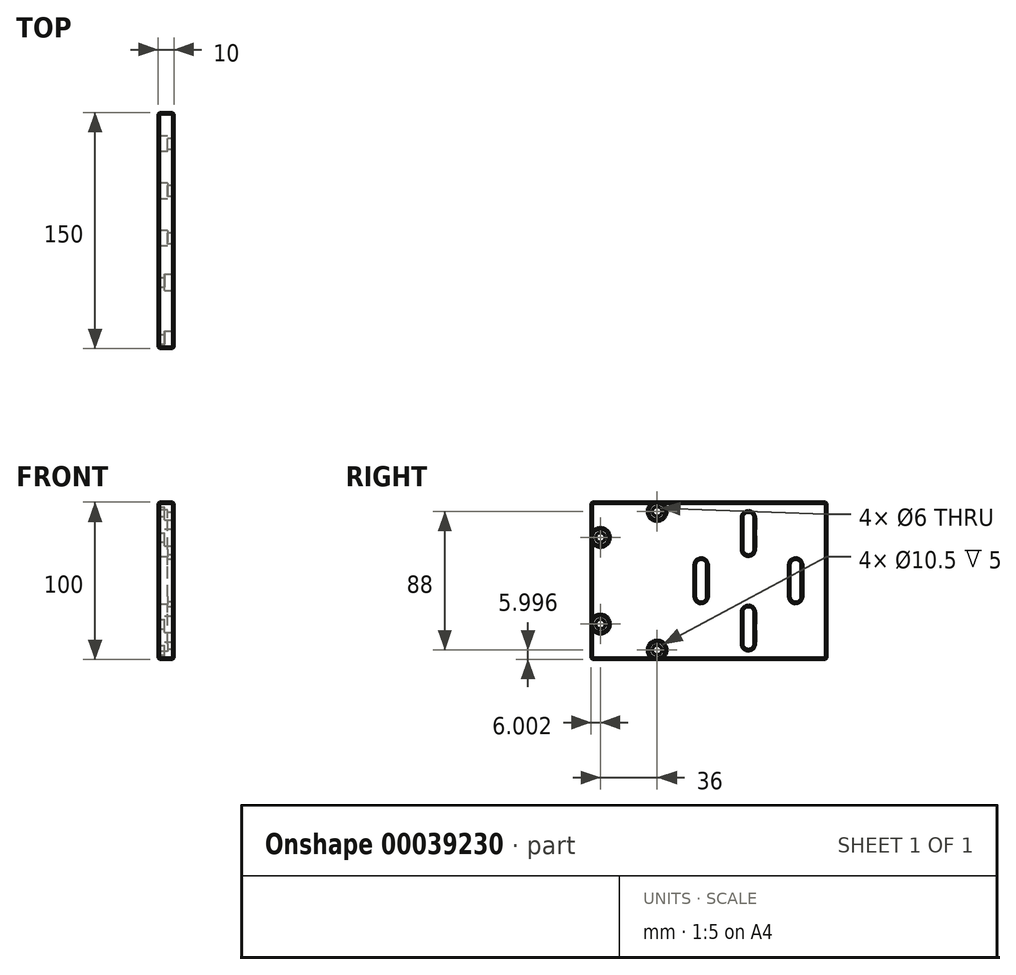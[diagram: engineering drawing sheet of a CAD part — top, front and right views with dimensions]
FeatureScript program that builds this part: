
annotation { "Feature Type Name" : "Feature", "Feature Type Description" : "" }
export const myFeature = defineFeature(function(context is Context, id is Id, definition is map)
    precondition{}
    {
        {
            var Q0;
            Q0=qCreatedBy(makeId("Right.planeOp"),FACE);
            var sketch = newSketch(context, id + "F0", { "sketchPlane" : qUnion([Q0])});
            skLineSegment(sketch, "E0.bottom", {"start": v(-58.68, 47.94) * mm, "end": v(91.32, 47.94) * mm});
            skLineSegment(sketch, "E0.top", {"start": v(-58.68, -52.06) * mm, "end": v(91.32, -52.06) * mm});
            skLineSegment(sketch, "E0.left", {"start": v(-58.68, 47.94) * mm, "end": v(-58.68, -52.06) * mm});
            skLineSegment(sketch, "E0.right", {"start": v(91.32, 47.94) * mm, "end": v(91.32, -52.06) * mm});
            skSolve(sketch);
        }
        {
            var Q0;
            Q0=makeQuery(id+"F0.imprint","IMPRINT",FACE,{"disambiguationData":[TD([[makeQuery(id+"F0.imprint","IMPRINT",EDGE,{"derivedFrom":sQuery(id+"F0.wireOp",EDGE,"E0.bottom")}),-1.0]])]});
            extrude(context, id + "F1", {"entities" : qUnion([Q0]), "depth" : 10 * mm});
        }
        {
            var Q0;
            Q0=makeQuery(id+"F1.opExtrude","CAP_FACE",FACE,{"disambiguationData":[OSD([sQuery(id+"F0.wireOp",EDGE,"E0.bottom"),sQuery(id+"F0.wireOp",EDGE,"E0.top"),sQuery(id+"F0.wireOp",EDGE,"E0.left"),sQuery(id+"F0.wireOp",EDGE,"E0.right")])],"isStart":false});
            var sketch = newSketch(context, id + "F2", { "sketchPlane" : qUnion([Q0])});
            skPoint(sketch, "E1", {"position": v(-52.68, 25.44) * mm});
            skPoint(sketch, "E2", {"position": v(-52.68, -29.56) * mm});
            skPoint(sketch, "E3", {"position": v(-16.68, 41.94) * mm});
            skPoint(sketch, "E4", {"position": v(-16.68, -46.06) * mm});
            skSolve(sketch);
        }
        {
            var Q0;
            Q0=sQuery(id+"F2.wireOp",VERTEX,"E3");
            var Q1;
            Q1=sQuery(id+"F2.wireOp",VERTEX,"E1");
            var Q2;
            Q2=sQuery(id+"F2.wireOp",VERTEX,"E2");
            var Q3;
            Q3=sQuery(id+"F2.wireOp",VERTEX,"E4");
            var Q4;
            Q4=makeQuery(id+"F1.opExtrude","SWEPT_BODY",BODY,{"disambiguationData":[OSD([sQuery(id+"F0.wireOp",EDGE,"E0.bottom"),sQuery(id+"F0.wireOp",EDGE,"E0.top"),sQuery(id+"F0.wireOp",EDGE,"E0.left"),sQuery(id+"F0.wireOp",EDGE,"E0.right")])]});
            hole(context, id + "F3", {"style" : HoleStyle.C_BORE, "holeDiameter" : 6 * mm, "cBoreDiameter" : 10.5 * mm, "cBoreDepth" : 6 * mm, "endStyle" : HoleEndStyle.THROUGH, "locations" : qUnion([Q0, Q1, Q2, Q3]), "scope" : qUnion([Q4])});
        }
        {
            var Q0;
            Q0=makeQuery(id+"F1.opExtrude","CAP_FACE",FACE,{"disambiguationData":[OSD([sQuery(id+"F0.wireOp",EDGE,"E0.bottom"),sQuery(id+"F0.wireOp",EDGE,"E0.top"),sQuery(id+"F0.wireOp",EDGE,"E0.left"),sQuery(id+"F0.wireOp",EDGE,"E0.right")])],"isStart":true});
            var sketch = newSketch(context, id + "F4", { "sketchPlane" : qUnion([Q0])});
            skPoint(sketch, "E5", {"position": v(-41.32, -2.06) * mm});
            skPoint(sketch, "E5.positionSnap0", {"position": v(-91.32, -2.06) * mm});
            skPoint(sketch, "E6", {"position": v(-11.32, -2.06) * mm});
            skPoint(sketch, "E7", {"position": v(-71.32, -2.06) * mm});
            skPoint(sketch, "E8", {"position": v(-41.32, 27.94) * mm});
            skPoint(sketch, "E9", {"position": v(-41.32, -32.06) * mm});
            skSolve(sketch);
        }
        {
            var Q0;
            {var subQ0=sQuery(id+"F0.wireOp",EDGE,"E0.bottom");Q0=makeQuery(id+"F4.imprint","IMPRINT",FACE,{"disambiguationData":[TD([[makeQuery(id+"F4.imprint","IMPRINT",EDGE,{"derivedFrom":makeQuery(id+"F1.opExtrude","CAP_EDGE",EDGE,{"disambiguationData":[OSD([subQ0])],"isStart":true})}),1.0]])]});}
            var sketch = newSketch(context, id + "F5", { "sketchPlane" : qUnion([Q0])});
            skLineSegment(sketch, "E10.left", {"start": v(-44.82, 37.94) * mm, "end": v(-44.82, 17.94) * mm});
            skLineSegment(sketch, "E10.right", {"start": v(-37.82, 37.94) * mm, "end": v(-37.82, 17.94) * mm});
            skArc(sketch, "E11", {"start": v(-37.82, 37.94) * mm, "mid": v(-41.32, 41.44) * mm, "end": v(-44.82, 37.94) * mm});
            skArc(sketch, "E12", {"start": v(-44.82, 17.94) * mm, "mid": v(-41.32, 14.44) * mm, "end": v(-37.82, 17.94) * mm});
            skArc(sketch, "E13", {"start": v(-67.82, 7.94) * mm, "mid": v(-71.32, 11.44) * mm, "end": v(-74.82, 7.94) * mm});
            skLineSegment(sketch, "E14.right", {"start": v(-67.82, 7.94) * mm, "end": v(-67.82, -12.06) * mm});
            skArc(sketch, "E15", {"start": v(-74.82, -12.06) * mm, "mid": v(-71.32, -15.56) * mm, "end": v(-67.82, -12.06) * mm});
            skLineSegment(sketch, "E14.left", {"start": v(-74.82, 7.94) * mm, "end": v(-74.82, -12.06) * mm});
            skArc(sketch, "E16", {"start": v(-7.82, 7.94) * mm, "mid": v(-11.32, 11.44) * mm, "end": v(-14.82, 7.94) * mm});
            skLineSegment(sketch, "E17.right", {"start": v(-7.82, 7.94) * mm, "end": v(-7.82, -12.06) * mm});
            skArc(sketch, "E18", {"start": v(-14.82, -12.06) * mm, "mid": v(-11.32, -15.56) * mm, "end": v(-7.82, -12.06) * mm});
            skLineSegment(sketch, "E17.left", {"start": v(-14.82, 7.94) * mm, "end": v(-14.82, -12.06) * mm});
            skArc(sketch, "E19", {"start": v(-37.82, -22.06) * mm, "mid": v(-41.32, -18.56) * mm, "end": v(-44.82, -22.06) * mm});
            skLineSegment(sketch, "E20.right", {"start": v(-37.82, -22.06) * mm, "end": v(-37.82, -42.06) * mm});
            skArc(sketch, "E21", {"start": v(-44.82, -42.06) * mm, "mid": v(-41.32, -45.56) * mm, "end": v(-37.82, -42.06) * mm});
            skLineSegment(sketch, "E20.left", {"start": v(-44.82, -22.06) * mm, "end": v(-44.82, -42.06) * mm});
            skSolve(sketch);
        }
        {
            var Q0;
            Q0=makeQuery(id+"F5.imprint","IMPRINT",FACE,{"disambiguationData":[TD([[makeQuery(id+"F5.imprint","IMPRINT",EDGE,{"derivedFrom":sQuery(id+"F5.wireOp",EDGE,"E13")}),1.0]])]});
            var Q1;
            Q1=makeQuery(id+"F5.imprint","IMPRINT",FACE,{"disambiguationData":[TD([[makeQuery(id+"F5.imprint","IMPRINT",EDGE,{"derivedFrom":sQuery(id+"F5.wireOp",EDGE,"E16")}),1.0]])]});
            var Q2;
            Q2=makeQuery(id+"F5.imprint","IMPRINT",FACE,{"disambiguationData":[TD([[makeQuery(id+"F5.imprint","IMPRINT",EDGE,{"derivedFrom":sQuery(id+"F5.wireOp",EDGE,"E19")}),1.0]])]});
            var Q3;
            Q3=makeQuery(id+"F5.imprint","IMPRINT",FACE,{"disambiguationData":[TD([[makeQuery(id+"F5.imprint","IMPRINT",EDGE,{"derivedFrom":sQuery(id+"F5.wireOp",EDGE,"E10.left")}),1.0]])]});
            extrude(context, id + "F6", {"entities" : qUnion([Q0, Q1, Q2, Q3]), "operationType" : NewBodyOperationType.REMOVE, "endBound" : BoundingType.THROUGH_ALL, "oppositeDirection" : true, "depth" : 25 * mm});
        }
        {
            var Q0;
            {var subQ0=sQuery(id+"F0.wireOp",EDGE,"E0.bottom");Q0=makeQuery(id+"F4.imprint","IMPRINT",FACE,{"disambiguationData":[TD([[makeQuery(id+"F4.imprint","IMPRINT",EDGE,{"derivedFrom":makeQuery(id+"F1.opExtrude","CAP_EDGE",EDGE,{"disambiguationData":[OSD([subQ0])],"isStart":true})}),1.0]])]});}
            var sketch = newSketch(context, id + "F7", { "sketchPlane" : qUnion([Q0])});
            skLineSegment(sketch, "E22.left", {"start": v(-76.32, 7.94) * mm, "end": v(-76.32, -12.06) * mm});
            skLineSegment(sketch, "E22.right", {"start": v(-66.32, 7.94) * mm, "end": v(-66.32, -12.06) * mm});
            skArc(sketch, "E23", {"start": v(-66.32, 7.94) * mm, "mid": v(-71.32, 12.94) * mm, "end": v(-76.32, 7.94) * mm});
            skArc(sketch, "E24", {"start": v(-76.32, -12.06) * mm, "mid": v(-71.32, -17.06) * mm, "end": v(-66.32, -12.06) * mm});
            skLineSegment(sketch, "E25.right", {"start": v(-36.32, -22.06) * mm, "end": v(-36.32, -42.06) * mm});
            skLineSegment(sketch, "E25.left", {"start": v(-46.32, -22.06) * mm, "end": v(-46.32, -42.06) * mm});
            skArc(sketch, "E26", {"start": v(-46.32, -42.06) * mm, "mid": v(-41.32, -47.06) * mm, "end": v(-36.32, -42.06) * mm});
            skArc(sketch, "E27", {"start": v(-36.32, -22.06) * mm, "mid": v(-41.32, -17.06) * mm, "end": v(-46.32, -22.06) * mm});
            skLineSegment(sketch, "E28.right", {"start": v(-6.32, 7.94) * mm, "end": v(-6.32, -12.06) * mm});
            skLineSegment(sketch, "E28.left", {"start": v(-16.32, 7.94) * mm, "end": v(-16.32, -12.06) * mm});
            skArc(sketch, "E29", {"start": v(-16.32, -12.06) * mm, "mid": v(-11.32, -17.06) * mm, "end": v(-6.32, -12.06) * mm});
            skArc(sketch, "E30", {"start": v(-6.32, 7.94) * mm, "mid": v(-11.32, 12.94) * mm, "end": v(-16.32, 7.94) * mm});
            skLineSegment(sketch, "E31.right", {"start": v(-36.32, 37.94) * mm, "end": v(-36.32, 17.94) * mm});
            skLineSegment(sketch, "E31.left", {"start": v(-46.32, 37.94) * mm, "end": v(-46.32, 17.94) * mm});
            skArc(sketch, "E32", {"start": v(-46.32, 17.94) * mm, "mid": v(-41.32, 12.94) * mm, "end": v(-36.32, 17.94) * mm});
            skArc(sketch, "E33", {"start": v(-36.32, 37.94) * mm, "mid": v(-41.32, 42.94) * mm, "end": v(-46.32, 37.94) * mm});
            skSolve(sketch);
        }
        {
            var Q0;
            Q0 = qSketchRegion(id + "F7", true);
            extrude(context, id + "F8", {"entities" : qUnion([Q0]), "operationType" : NewBodyOperationType.REMOVE, "oppositeDirection" : true, "depth" : 6 * mm});
        }
        {
            var Q0;
            Q0=makeQuery(id+"F1.opExtrude","CAP_EDGE",EDGE,{"disambiguationData":[OSD([sQuery(id+"F0.wireOp",EDGE,"E0.right")])],"isStart":true});
            var Q1;
            Q1=makeQuery(id+"F1.opExtrude","CAP_EDGE",EDGE,{"disambiguationData":[OSD([sQuery(id+"F0.wireOp",EDGE,"E0.right")])],"isStart":false});
            var Q2;
            Q2=makeQuery(id+"F1.opExtrude","SWEPT_EDGE",EDGE,{"disambiguationData":[OSD([sQuery(id+"F0.wireOp",EDGE,"E0.top"),sQuery(id+"F0.wireOp",EDGE,"E0.right")])]});
            var Q3;
            Q3=makeQuery(id+"F1.opExtrude","CAP_EDGE",EDGE,{"disambiguationData":[OSD([sQuery(id+"F0.wireOp",EDGE,"E0.top")])],"isStart":true});
            var Q4;
            Q4=makeQuery(id+"F1.opExtrude","CAP_EDGE",EDGE,{"disambiguationData":[OSD([sQuery(id+"F0.wireOp",EDGE,"E0.top")])],"isStart":false});
            var Q5;
            Q5=makeQuery(id+"F1.opExtrude","CAP_EDGE",EDGE,{"disambiguationData":[OSD([sQuery(id+"F0.wireOp",EDGE,"E0.bottom")])],"isStart":true});
            var Q6;
            Q6=makeQuery(id+"F1.opExtrude","SWEPT_EDGE",EDGE,{"disambiguationData":[OSD([sQuery(id+"F0.wireOp",EDGE,"E0.bottom"),sQuery(id+"F0.wireOp",EDGE,"E0.right")])]});
            var Q7;
            Q7=makeQuery(id+"F8.boolean.opBoolean","COPY",EDGE,{"derivedFrom":makeQuery(id+"F8.opExtrude","CAP_EDGE",EDGE,{"disambiguationData":[OSD([sQuery(id+"F7.wireOp",EDGE,"E22.right")])],"isStart":true})});
            var Q8;
            Q8=makeQuery(id+"F8.boolean.opBoolean","COPY",EDGE,{"derivedFrom":makeQuery(id+"F8.opExtrude","CAP_EDGE",EDGE,{"disambiguationData":[OSD([sQuery(id+"F7.wireOp",EDGE,"E22.left")])],"isStart":true})});
            var Q9;
            Q9=makeQuery(id+"F8.boolean.opBoolean","COPY",EDGE,{"derivedFrom":makeQuery(id+"F8.opExtrude","CAP_EDGE",EDGE,{"disambiguationData":[OSD([sQuery(id+"F7.wireOp",EDGE,"E23")])],"isStart":true})});
            var Q10;
            Q10=makeQuery(id+"F8.boolean.opBoolean","COPY",EDGE,{"derivedFrom":makeQuery(id+"F8.opExtrude","CAP_EDGE",EDGE,{"disambiguationData":[OSD([sQuery(id+"F7.wireOp",EDGE,"E24")])],"isStart":true})});
            var Q11;
            Q11=makeQuery(id+"F8.boolean.opBoolean","COPY",EDGE,{"derivedFrom":makeQuery(id+"F8.opExtrude","CAP_EDGE",EDGE,{"disambiguationData":[OSD([sQuery(id+"F7.wireOp",EDGE,"E31.left")])],"isStart":true})});
            var Q12;
            Q12=makeQuery(id+"F8.boolean.opBoolean","COPY",EDGE,{"derivedFrom":makeQuery(id+"F8.opExtrude","CAP_EDGE",EDGE,{"disambiguationData":[OSD([sQuery(id+"F7.wireOp",EDGE,"E31.right")])],"isStart":true})});
            var Q13;
            Q13=makeQuery(id+"F8.boolean.opBoolean","COPY",EDGE,{"derivedFrom":makeQuery(id+"F8.opExtrude","CAP_EDGE",EDGE,{"disambiguationData":[OSD([sQuery(id+"F7.wireOp",EDGE,"E33")])],"isStart":true})});
            var Q14;
            Q14=makeQuery(id+"F8.boolean.opBoolean","COPY",EDGE,{"derivedFrom":makeQuery(id+"F8.opExtrude","CAP_EDGE",EDGE,{"disambiguationData":[OSD([sQuery(id+"F7.wireOp",EDGE,"E32")])],"isStart":true})});
            var Q15;
            Q15=makeQuery(id+"F8.boolean.opBoolean","COPY",EDGE,{"derivedFrom":makeQuery(id+"F8.opExtrude","CAP_EDGE",EDGE,{"disambiguationData":[OSD([sQuery(id+"F7.wireOp",EDGE,"E25.right")])],"isStart":true})});
            var Q16;
            Q16=makeQuery(id+"F8.boolean.opBoolean","COPY",EDGE,{"derivedFrom":makeQuery(id+"F8.opExtrude","CAP_EDGE",EDGE,{"disambiguationData":[OSD([sQuery(id+"F7.wireOp",EDGE,"E27")])],"isStart":true})});
            var Q17;
            Q17=makeQuery(id+"F8.boolean.opBoolean","COPY",EDGE,{"derivedFrom":makeQuery(id+"F8.opExtrude","CAP_EDGE",EDGE,{"disambiguationData":[OSD([sQuery(id+"F7.wireOp",EDGE,"E25.left")])],"isStart":true})});
            var Q18;
            Q18=makeQuery(id+"F8.boolean.opBoolean","COPY",EDGE,{"derivedFrom":makeQuery(id+"F8.opExtrude","CAP_EDGE",EDGE,{"disambiguationData":[OSD([sQuery(id+"F7.wireOp",EDGE,"E26")])],"isStart":true})});
            var Q19;
            Q19=makeQuery(id+"F8.boolean.opBoolean","COPY",EDGE,{"derivedFrom":makeQuery(id+"F8.opExtrude","CAP_EDGE",EDGE,{"disambiguationData":[OSD([sQuery(id+"F7.wireOp",EDGE,"E29")])],"isStart":true})});
            var Q20;
            Q20=makeQuery(id+"F8.boolean.opBoolean","COPY",EDGE,{"derivedFrom":makeQuery(id+"F8.opExtrude","CAP_EDGE",EDGE,{"disambiguationData":[OSD([sQuery(id+"F7.wireOp",EDGE,"E28.right")])],"isStart":true})});
            var Q21;
            Q21=makeQuery(id+"F8.boolean.opBoolean","COPY",EDGE,{"derivedFrom":makeQuery(id+"F8.opExtrude","CAP_EDGE",EDGE,{"disambiguationData":[OSD([sQuery(id+"F7.wireOp",EDGE,"E28.left")])],"isStart":true})});
            var Q22;
            Q22=makeQuery(id+"F8.boolean.opBoolean","COPY",EDGE,{"derivedFrom":makeQuery(id+"F8.opExtrude","CAP_EDGE",EDGE,{"disambiguationData":[OSD([sQuery(id+"F7.wireOp",EDGE,"E30")])],"isStart":true})});
            var Q23;
            Q23=makeQuery(id+"F3.hole-0.boolean.opBoolean","INTERSECT",EDGE,{"derivedFrom":[makeQuery(id+"F1.opExtrude","CAP_FACE",FACE,{"disambiguationData":[OSD([sQuery(id+"F0.wireOp",EDGE,"E0.bottom"),sQuery(id+"F0.wireOp",EDGE,"E0.top"),sQuery(id+"F0.wireOp",EDGE,"E0.left"),sQuery(id+"F0.wireOp",EDGE,"E0.right")])],"isStart":true}),makeQuery(id+"F3.hole-0.opRevolve","SWEPT_FACE",FACE,{"disambiguationData":[OSD([sQuery(id+"F3.hole-0.sketch.wireOp",EDGE,"core_line_2")])]})]});
            var Q24;
            Q24=makeQuery(id+"F3.hole-1.boolean.opBoolean","INTERSECT",EDGE,{"derivedFrom":[makeQuery(id+"F1.opExtrude","CAP_FACE",FACE,{"disambiguationData":[OSD([sQuery(id+"F0.wireOp",EDGE,"E0.bottom"),sQuery(id+"F0.wireOp",EDGE,"E0.top"),sQuery(id+"F0.wireOp",EDGE,"E0.left"),sQuery(id+"F0.wireOp",EDGE,"E0.right")])],"isStart":true}),makeQuery(id+"F3.hole-1.opRevolve","SWEPT_FACE",FACE,{"disambiguationData":[OSD([sQuery(id+"F3.hole-1.sketch.wireOp",EDGE,"core_line_2")])]})]});
            var Q25;
            Q25=makeQuery(id+"F3.hole-2.boolean.opBoolean","INTERSECT",EDGE,{"derivedFrom":[makeQuery(id+"F1.opExtrude","CAP_FACE",FACE,{"disambiguationData":[OSD([sQuery(id+"F0.wireOp",EDGE,"E0.bottom"),sQuery(id+"F0.wireOp",EDGE,"E0.top"),sQuery(id+"F0.wireOp",EDGE,"E0.left"),sQuery(id+"F0.wireOp",EDGE,"E0.right")])],"isStart":true}),makeQuery(id+"F3.hole-2.opRevolve","SWEPT_FACE",FACE,{"disambiguationData":[OSD([sQuery(id+"F3.hole-2.sketch.wireOp",EDGE,"core_line_2")])]})]});
            var Q26;
            Q26=makeQuery(id+"F3.hole-3.boolean.opBoolean","INTERSECT",EDGE,{"derivedFrom":[makeQuery(id+"F1.opExtrude","CAP_FACE",FACE,{"disambiguationData":[OSD([sQuery(id+"F0.wireOp",EDGE,"E0.bottom"),sQuery(id+"F0.wireOp",EDGE,"E0.top"),sQuery(id+"F0.wireOp",EDGE,"E0.left"),sQuery(id+"F0.wireOp",EDGE,"E0.right")])],"isStart":true}),makeQuery(id+"F3.hole-3.opRevolve","SWEPT_FACE",FACE,{"disambiguationData":[OSD([sQuery(id+"F3.hole-3.sketch.wireOp",EDGE,"core_line_2")])]})]});
            var Q27;
            Q27=makeQuery(id+"F1.opExtrude","SWEPT_EDGE",EDGE,{"disambiguationData":[OSD([sQuery(id+"F0.wireOp",EDGE,"E0.top"),sQuery(id+"F0.wireOp",EDGE,"E0.left")])]});
            var Q28;
            Q28=makeQuery(id+"F1.opExtrude","CAP_EDGE",EDGE,{"disambiguationData":[OSD([sQuery(id+"F0.wireOp",EDGE,"E0.left")])],"isStart":true});
            var Q29;
            Q29=makeQuery(id+"F1.opExtrude","SWEPT_EDGE",EDGE,{"disambiguationData":[OSD([sQuery(id+"F0.wireOp",EDGE,"E0.bottom"),sQuery(id+"F0.wireOp",EDGE,"E0.left")])]});
            var Q30;
            Q30=makeQuery(id+"F1.opExtrude","CAP_EDGE",EDGE,{"disambiguationData":[OSD([sQuery(id+"F0.wireOp",EDGE,"E0.left")])],"isStart":false});
            var Q31;
            Q31=makeQuery(id+"F1.opExtrude","CAP_EDGE",EDGE,{"disambiguationData":[OSD([sQuery(id+"F0.wireOp",EDGE,"E0.bottom")])],"isStart":false});
            var Q32;
            Q32=makeQuery(id+"F3.hole-0.boolean.opBoolean","COPY",EDGE,{"derivedFrom":makeQuery(id+"F3.hole-0.opRevolve","SWEPT_EDGE",EDGE,{"disambiguationData":[OSD([sQuery(id+"F3.hole-0.sketch.wireOp",EDGE,"cbore_start_line_2"),sQuery(id+"F3.hole-0.sketch.wireOp",EDGE,"cbore_start_line_3")])]})});
            var Q33;
            Q33=makeQuery(id+"F3.hole-1.boolean.opBoolean","COPY",EDGE,{"derivedFrom":makeQuery(id+"F3.hole-1.opRevolve","SWEPT_EDGE",EDGE,{"disambiguationData":[OSD([sQuery(id+"F3.hole-1.sketch.wireOp",EDGE,"cbore_start_line_2"),sQuery(id+"F3.hole-1.sketch.wireOp",EDGE,"cbore_start_line_3")])]})});
            var Q34;
            Q34=makeQuery(id+"F3.hole-2.boolean.opBoolean","COPY",EDGE,{"derivedFrom":makeQuery(id+"F3.hole-2.opRevolve","SWEPT_EDGE",EDGE,{"disambiguationData":[OSD([sQuery(id+"F3.hole-2.sketch.wireOp",EDGE,"cbore_start_line_2"),sQuery(id+"F3.hole-2.sketch.wireOp",EDGE,"cbore_start_line_3")])]})});
            var Q35;
            Q35=makeQuery(id+"F3.hole-3.boolean.opBoolean","COPY",EDGE,{"derivedFrom":makeQuery(id+"F3.hole-3.opRevolve","SWEPT_EDGE",EDGE,{"disambiguationData":[OSD([sQuery(id+"F3.hole-3.sketch.wireOp",EDGE,"cbore_start_line_2"),sQuery(id+"F3.hole-3.sketch.wireOp",EDGE,"cbore_start_line_3")])]})});
            var Q36;
            Q36=makeQuery(id+"F6.boolean.opBoolean","INTERSECT",EDGE,{"derivedFrom":[makeQuery(id+"F1.opExtrude","CAP_FACE",FACE,{"disambiguationData":[OSD([sQuery(id+"F0.wireOp",EDGE,"E0.bottom"),sQuery(id+"F0.wireOp",EDGE,"E0.top"),sQuery(id+"F0.wireOp",EDGE,"E0.left"),sQuery(id+"F0.wireOp",EDGE,"E0.right")])],"isStart":false}),makeQuery(id+"F6.opExtrude","SWEPT_FACE",FACE,{"disambiguationData":[OSD([sQuery(id+"F5.wireOp",EDGE,"E17.left")])]})]});
            var Q37;
            Q37=makeQuery(id+"F6.boolean.opBoolean","INTERSECT",EDGE,{"derivedFrom":[makeQuery(id+"F1.opExtrude","CAP_FACE",FACE,{"disambiguationData":[OSD([sQuery(id+"F0.wireOp",EDGE,"E0.bottom"),sQuery(id+"F0.wireOp",EDGE,"E0.top"),sQuery(id+"F0.wireOp",EDGE,"E0.left"),sQuery(id+"F0.wireOp",EDGE,"E0.right")])],"isStart":false}),makeQuery(id+"F6.opExtrude","SWEPT_FACE",FACE,{"disambiguationData":[OSD([sQuery(id+"F5.wireOp",EDGE,"E16")])]})]});
            var Q38;
            Q38=makeQuery(id+"F1.opExtrude","CAP_FACE",FACE,{"disambiguationData":[OSD([sQuery(id+"F0.wireOp",EDGE,"E0.bottom"),sQuery(id+"F0.wireOp",EDGE,"E0.top"),sQuery(id+"F0.wireOp",EDGE,"E0.left"),sQuery(id+"F0.wireOp",EDGE,"E0.right")])],"isStart":false});
            chamfer(context, id + "F9", {"entities" : qUnion([Q0, Q1, Q2, Q3, Q4, Q5, Q6, Q7, Q8, Q9, Q10, Q11, Q12, Q13, Q14, Q15, Q16, Q17, Q18, Q19, Q20, Q21, Q22, Q23, Q24, Q25, Q26, Q27, Q28, Q29, Q30, Q31, Q32, Q33, Q34, Q35, Q36, Q37, Q38]), "width" : 1 * mm, "tangentPropagation" : true});
        }
    });
